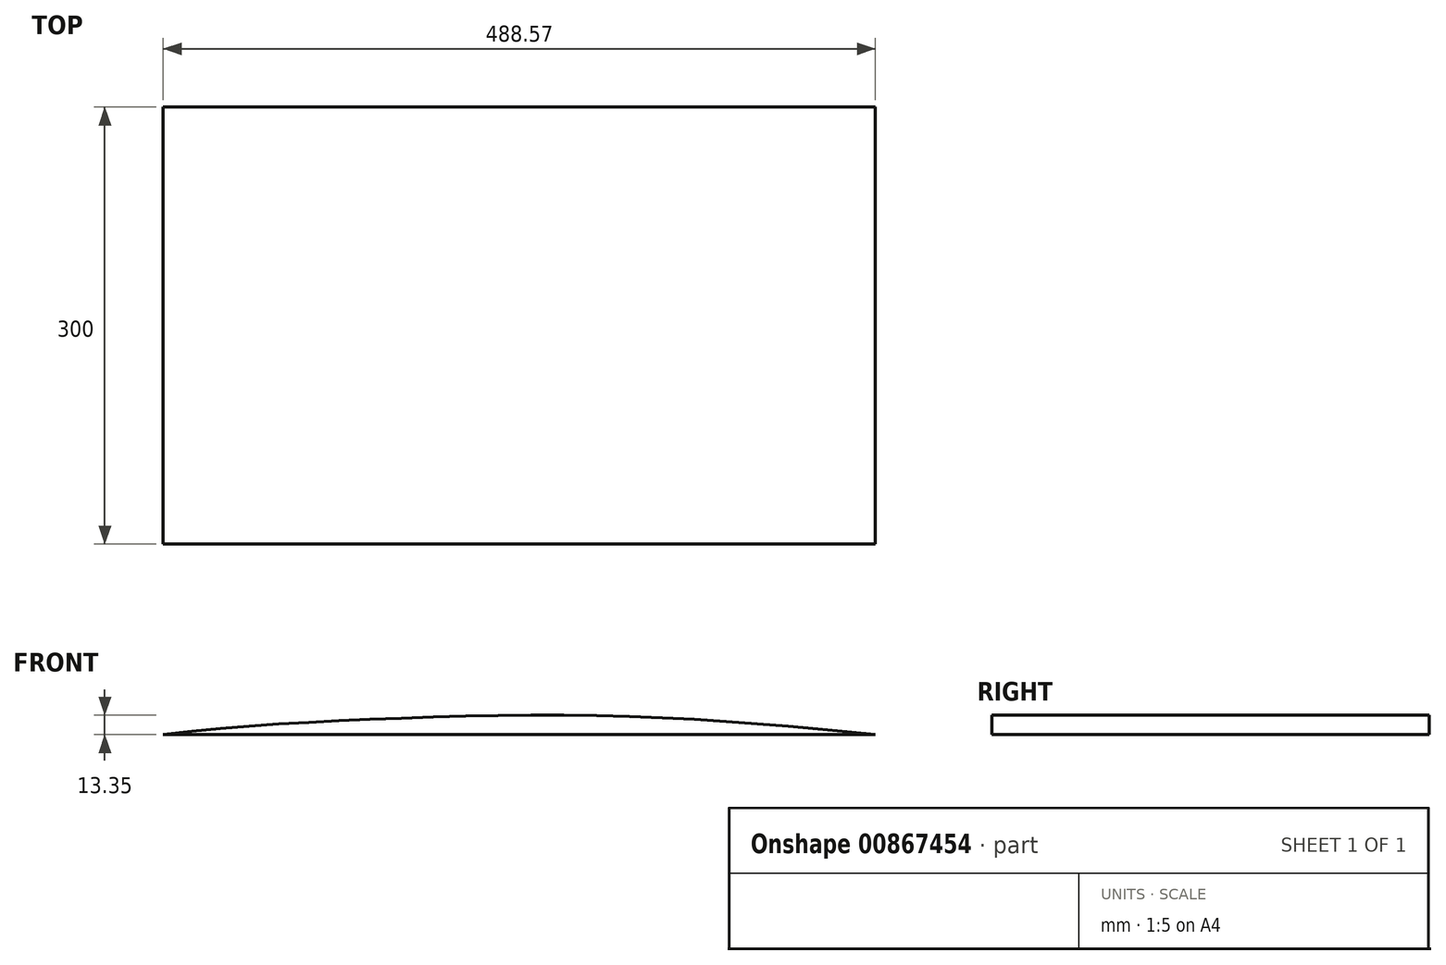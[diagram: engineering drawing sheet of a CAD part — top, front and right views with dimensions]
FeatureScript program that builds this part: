
annotation { "Feature Type Name" : "Feature", "Feature Type Description" : "" }
export const myFeature = defineFeature(function(context is Context, id is Id, definition is map)
    precondition{}
    {
        {
            var Q0;
            Q0=qCreatedBy(makeId("Front.planeOp"),FACE);
            var sketch = newSketch(context, id + "F0", { "sketchPlane" : qUnion([Q0])});
            skLineSegment(sketch, "E0", {"start": v(0, 0) * mm, "end": v(488.57, 0) * mm});
            skFitSpline(sketch, "E1", {"points": [v(488.57, 0) * mm, v(328.92, 12.19) * mm, v(149.23, 10.86) * mm, v(0, 0) * mm], "startDerivative": vector(-437.51, 44.43) * mm, "endDerivative": vector(-444.86, -54.63) * mm});
            skSolve(sketch);
        }
        {
            var Q0;
            Q0=makeQuery(id+"F0.imprint","IMPRINT",FACE,{"disambiguationData":[TD([[makeQuery(id+"F0.imprint","IMPRINT",EDGE,{"derivedFrom":sQuery(id+"F0.wireOp",EDGE,"E0")}),1.0]])]});
            extrude(context, id + "F1", {"entities" : qUnion([Q0]), "endBound" : BoundingType.SYMMETRIC, "depth" : 300 * mm, "offsetDistance" : 25 * mm});
        }
    });
